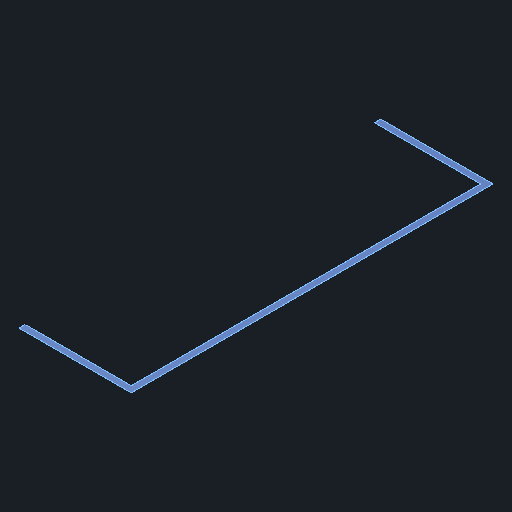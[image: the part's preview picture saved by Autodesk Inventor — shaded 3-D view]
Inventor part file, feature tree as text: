
AUTODESK INVENTOR PART (.ipt)
format: ipt  version: 2025 (Build 290162000, 162)  size: 80,896 bytes
history: native  units: in
note: dims shown in document units (in); Inventor stores cm internally (conversion verified against a paired STEP export)
features: extrude x1
ambient origin geometry x8: Origin, YZ Plane, XZ Plane, XY Plane, X Axis, Y Axis, Z Axis, Center Point
bodies: Solid1 (feature_tree)
feature tree (1):
  extrude  "Extrude-Thin1"  [1 undecoded]
note: 1 required parameter value undecoded (feature->parameter linkage not recoverable at this tier; creation-order binding heuristic only, values carry confidence <= 0.55)
